# Revit family: VLGFS100xxOSxx
name_source: partatom
category: Leuchten
units: mm (PartAtom-declared; Revit-internal decimal feet)

## family parameters
Basisbauteil = Fläche
Beim Laden mit Abzugskörper schneiden = Nein
Bemaßung runder Anschluss = Durchmesser verwenden
Gemeinsam genutzt = Nein
Lichtquelle = Ja
OmniClass-Nummer = 23.80.70.11
OmniClass-Titel = Luminaries for Internal Lighting
Raumberechnungspunkt = Nein
Teiletyp = Normal

## types (16) — shared parameters
Baugruppenkennzeichen = D5020200
Datei für fotometrisches Netz = VLGFS1xxxOS.IES
Emissionsform beim Rendern sichtbar = Nein
Farbfilter = 16777215
Farbtemperaturverschiebung bei Dämpfen der Lampe = <Keine Auswahl>
Hersteller = RIDI Leuchten GmbH
Lampe = LED
Neigungswinkel = 90.00°
URL = www.ridi.de
Von Breite des Rechtecks ausssenden = 977 mm  [stored 3.20538 ft]
Von Länge des Rechtecks aussenden = 94 mm  [stored 0.308399 ft]
brand = RIDI
conformity mark = CE
electrical safety class = 1
height = 74 mm  [stored 0.242782 ft]
ingress protection (IP) code = IP54
length = 1000 mm  [stored 3.28084 ft]
nominal frequency = 50-60Hz
nominal voltage = 230
voltage type (AC, DC, UC) = AC
width = 97 mm  [stored 0.318241 ft]
zero-valued in all types: Vorgabe-Ansicht

## per-type parameters (varying)
| type | Modell | Scheinlast | rated input power | weight |
| VLGFS1001-5NDWS830OS0500 | 1551197 | 41 VA | 41 | 2,08 kg |
| VLGFS1001-5NDWS840OS0500 | 1551194 | 41 VA | 41 | 2,08 kg |
| VLGFS1001-5NDWS850OS0500 | 1551200 | 41 VA | 41 | 2,08 kg |
| VLGFS1001-5NDWS865OS0500 | 1551203 | 41 VA | 41 | 2,08 kg |
| VLGFS1001-7DAWS830OS0500 | 1561197 | 41 VA | 41 | 2,08 kg |
| VLGFS1001-7DAWS840OS0500 | 1561194 | 41 VA | 41 | 2,08 kg |
| VLGFS1001-7DAWS850OS0500 | 1561200 | 41 VA | 41 | 2,08 kg |
| VLGFS1001-7DAWS865OS0500 | 1561203 | 41 VA | 41 | 2,08 kg |
| VLGFS1002-5NDWS830OS0950 | 1551252 | 78 VA | 78 | 2,17 kg |
| VLGFS1002-5NDWS840OS1000 | 1551249 | 78 VA | 78 | 2,17 kg |
| VLGFS1002-5NDWS850OS1000 | 1551255 | 78 VA | 78 | 2,17 kg |
| VLGFS1002-5NDWS865OS1000 | 1551258 | 78 VA | 78 | 2,17 kg |
| VLGFS1002-7DAWS830OS0950 | 1561252 | 78 VA | 78 | 2,17 kg |
| VLGFS1002-7DAWS840OS1000 | 1561249 | 78 VA | 78 | 2,17 kg |
| VLGFS1002-7DAWS850OS1000 | 1561255 | 78 VA | 78 | 2,17 kg |
| VLGFS1002-7DAWS865OS1000 | 1561258 | 78 VA | 78 | 2,17 kg |

note: column(s) folded — value = type name in every type: product name

note: [stored X ft] marks values corroborated as IEEE doubles in the binary element streams (Revit-internal decimal feet)
